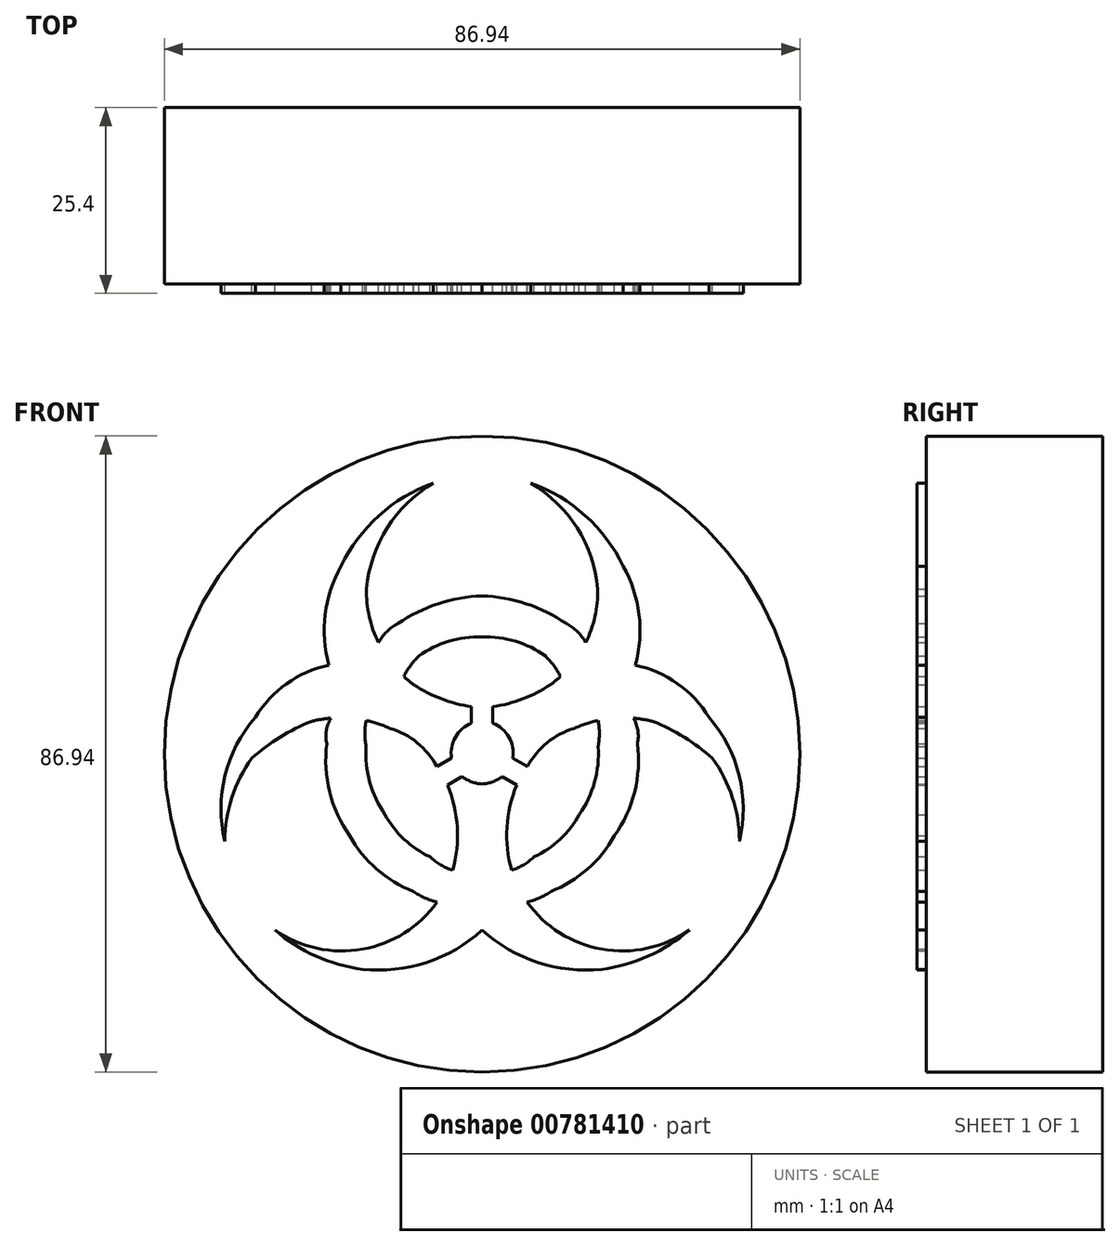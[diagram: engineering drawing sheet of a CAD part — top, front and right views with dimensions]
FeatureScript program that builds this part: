
annotation { "Feature Type Name" : "Feature", "Feature Type Description" : "" }
export const myFeature = defineFeature(function(context is Context, id is Id, definition is map)
    precondition{}
    {
        {
            var Q0;
            Q0=qCreatedBy(makeId("Front.planeOp"),FACE);
            var sketch = newSketch(context, id + "F0", { "sketchPlane" : qUnion([Q0])});
            skArc(sketch, "E0", {"start": v(-6.67, 37.02) * mm, "mid": v(-14.1, 32.6) * mm, "end": v(-19.3, 25.67) * mm});
            skArc(sketch, "E1", {"start": v(-19.3, 25.67) * mm, "mid": v(-21.46, 19.06) * mm, "end": v(-20.95, 12.14) * mm});
            skArc(sketch, "E2", {"start": v(-20.95, 12.14) * mm, "mid": v(-26.73, 9.61) * mm, "end": v(-31.03, 5) * mm});
            skArc(sketch, "E3", {"start": v(-31.03, 5) * mm, "mid": v(-35.17, -2.96) * mm, "end": v(-35.2, -11.93) * mm});
            skArc(sketch, "E4", {"start": v(-6.67, 37.02) * mm, "mid": v(-13, 30.9) * mm, "end": v(-15.81, 22.57) * mm});
            skArc(sketch, "E5", {"start": v(-15.81, 22.57) * mm, "mid": v(-14.17, 15.23) * mm, "end": v(-9.34, 9.47) * mm});
            skArc(sketch, "E6", {"start": v(-9.34, 9.47) * mm, "mid": v(-5.56, 7.53) * mm, "end": v(-1.45, 6.47) * mm});
            skLineSegment(sketch, "E7", {"start": v(-1.45, 6.47) * mm, "end": v(-1.45, 4.21) * mm});
            skArc(sketch, "E8", {"start": v(-1.45, 4.21) * mm, "mid": v(-3.66, 2.3) * mm, "end": v(-4.2, -0.59) * mm});
            skLineSegment(sketch, "E9", {"start": v(-4.2, -0.59) * mm, "end": v(-6.2, -1.7) * mm});
            skArc(sketch, "E10", {"start": v(-6.2, -1.7) * mm, "mid": v(-8.9, 1.55) * mm, "end": v(-12.64, 3.52) * mm});
            skArc(sketch, "E11", {"start": v(-12.64, 3.52) * mm, "mid": v(-17.9, 4.89) * mm, "end": v(-23.34, 4.46) * mm});
            skArc(sketch, "E12", {"start": v(-23.34, 4.46) * mm, "mid": v(-27.64, 2.3) * mm, "end": v(-31.5, -0.59) * mm});
            skArc(sketch, "E13", {"start": v(-31.5, -0.59) * mm, "mid": v(-34.24, -5.97) * mm, "end": v(-35.2, -11.93) * mm});
            skArc(sketch, "E14.MirrorCS", {"start": v(6.67, 37.02) * mm, "mid": v(14.1, 32.6) * mm, "end": v(19.3, 25.67) * mm});
            skArc(sketch, "E15.MirrorCS", {"start": v(6.67, 37.02) * mm, "mid": v(13, 30.9) * mm, "end": v(15.81, 22.57) * mm});
            skArc(sketch, "E16.MirrorCS", {"start": v(15.81, 22.57) * mm, "mid": v(14.17, 15.23) * mm, "end": v(9.34, 9.47) * mm});
            skArc(sketch, "E17.MirrorCS", {"start": v(19.3, 25.67) * mm, "mid": v(21.46, 19.06) * mm, "end": v(20.95, 12.14) * mm});
            skArc(sketch, "E18.MirrorCS", {"start": v(9.34, 9.47) * mm, "mid": v(5.56, 7.53) * mm, "end": v(1.45, 6.47) * mm});
            skArc(sketch, "E19.MirrorCS", {"start": v(6.2, -1.7) * mm, "mid": v(8.9, 1.55) * mm, "end": v(12.64, 3.52) * mm});
            skArc(sketch, "E20.MirrorCS", {"start": v(12.64, 3.52) * mm, "mid": v(17.9, 4.89) * mm, "end": v(23.34, 4.46) * mm});
            skArc(sketch, "E21.MirrorCS", {"start": v(23.34, 4.46) * mm, "mid": v(27.64, 2.3) * mm, "end": v(31.5, -0.59) * mm});
            skArc(sketch, "E22.MirrorCS", {"start": v(20.95, 12.14) * mm, "mid": v(26.73, 9.61) * mm, "end": v(31.03, 5) * mm});
            skArc(sketch, "E23.MirrorCS", {"start": v(31.03, 5) * mm, "mid": v(35.17, -2.96) * mm, "end": v(35.2, -11.93) * mm});
            skArc(sketch, "E24.MirrorCS", {"start": v(31.5, -0.59) * mm, "mid": v(34.24, -5.97) * mm, "end": v(35.2, -11.93) * mm});
            skLineSegment(sketch, "E25.MirrorCS", {"start": v(4.2, -0.59) * mm, "end": v(6.2, -1.7) * mm});
            skArc(sketch, "E26.MirrorCS", {"start": v(1.45, 4.21) * mm, "mid": v(3.66, 2.3) * mm, "end": v(4.2, -0.59) * mm});
            skLineSegment(sketch, "E27.MirrorCS", {"start": v(1.45, 6.47) * mm, "end": v(1.45, 4.21) * mm});
            skArc(sketch, "E28", {"start": v(0, 21.6) * mm, "mid": v(-6.03, 20.54) * mm, "end": v(-11.5, 17.82) * mm});
            skArc(sketch, "E29.MirrorCS", {"start": v(0, 21.6) * mm, "mid": v(6.03, 20.54) * mm, "end": v(11.5, 17.82) * mm});
            skArc(sketch, "E30", {"start": v(-11.5, 17.82) * mm, "mid": v(-13.04, 16.72) * mm, "end": v(-14.17, 15.23) * mm});
            skArc(sketch, "E31", {"start": v(0, 15.99) * mm, "mid": v(-4.55, 15.42) * mm, "end": v(-8.66, 13.38) * mm});
            skArc(sketch, "E32", {"start": v(-8.66, 13.38) * mm, "mid": v(-9.8, 12.08) * mm, "end": v(-10.7, 10.6) * mm});
            skArc(sketch, "E33.MirrorCS", {"start": v(0, 15.99) * mm, "mid": v(4.55, 15.42) * mm, "end": v(8.66, 13.38) * mm});
            skArc(sketch, "E34.MirrorCS", {"start": v(8.66, 13.38) * mm, "mid": v(9.8, 12.08) * mm, "end": v(10.7, 10.6) * mm});
            skArc(sketch, "E35.MirrorCS", {"start": v(11.5, 17.82) * mm, "mid": v(13.04, 16.72) * mm, "end": v(14.17, 15.23) * mm});
            skArc(sketch, "E36", {"start": v(-4.04, -15.94) * mm, "mid": v(-3.4, -10.05) * mm, "end": v(-4.73, -4.28) * mm});
            skArc(sketch, "E37", {"start": v(-16.35, -26.67) * mm, "mid": v(-8.7, -23.03) * mm, "end": v(-4.04, -15.94) * mm});
            skArc(sketch, "E38", {"start": v(-28.34, -24.07) * mm, "mid": v(-22.6, -26.57) * mm, "end": v(-16.35, -26.67) * mm});
            skArc(sketch, "E39", {"start": v(-28.34, -24.07) * mm, "mid": v(-22.75, -27.64) * mm, "end": v(-16.35, -29.43) * mm});
            skArc(sketch, "E40", {"start": v(-16.35, -29.43) * mm, "mid": v(-7.6, -28.5) * mm, "end": v(0, -24.07) * mm});
            skArc(sketch, "E41", {"start": v(-2.78, -3.08) * mm, "mid": v(-1.46, -3.79) * mm, "end": v(0, -4.1) * mm});
            skLineSegment(sketch, "E42", {"start": v(-4.73, -4.28) * mm, "end": v(-2.78, -3.08) * mm});
            skArc(sketch, "E43.MirrorCS", {"start": v(2.78, -3.08) * mm, "mid": v(1.46, -3.79) * mm, "end": v(0, -4.1) * mm});
            skLineSegment(sketch, "E44.MirrorCS", {"start": v(4.73, -4.28) * mm, "end": v(2.78, -3.08) * mm});
            skArc(sketch, "E45.MirrorCS", {"start": v(4.04, -15.94) * mm, "mid": v(3.4, -10.05) * mm, "end": v(4.73, -4.28) * mm});
            skArc(sketch, "E46.MirrorCS", {"start": v(16.35, -26.67) * mm, "mid": v(8.7, -23.03) * mm, "end": v(4.04, -15.94) * mm});
            skArc(sketch, "E47.MirrorCS", {"start": v(28.34, -24.07) * mm, "mid": v(22.6, -26.57) * mm, "end": v(16.35, -26.67) * mm});
            skArc(sketch, "E48.MirrorCS", {"start": v(28.34, -24.07) * mm, "mid": v(22.75, -27.64) * mm, "end": v(16.35, -29.43) * mm});
            skArc(sketch, "E49.MirrorCS", {"start": v(16.35, -29.43) * mm, "mid": v(7.6, -28.5) * mm, "end": v(0, -24.07) * mm});
            skArc(sketch, "E50", {"start": v(-15.88, 1.03) * mm, "mid": v(-15.37, -3.85) * mm, "end": v(-13.27, -8.29) * mm});
            skArc(sketch, "E51", {"start": v(-13.27, -8.29) * mm, "mid": v(-10.66, -11.67) * mm, "end": v(-7.12, -14.05) * mm});
            skArc(sketch, "E52", {"start": v(-7.12, -14.05) * mm, "mid": v(-5.68, -15.15) * mm, "end": v(-4.03, -15.9) * mm});
            skArc(sketch, "E53", {"start": v(-21.24, 1.42) * mm, "mid": v(-20.85, -5.18) * mm, "end": v(-18.1, -11.2) * mm});
            skArc(sketch, "E54", {"start": v(-18.1, -11.2) * mm, "mid": v(-14.42, -15.75) * mm, "end": v(-9.42, -18.79) * mm});
            skArc(sketch, "E55", {"start": v(-9.42, -18.79) * mm, "mid": v(-7.86, -19.67) * mm, "end": v(-6.17, -20.24) * mm});
            skArc(sketch, "E56", {"start": v(-20.7, 4.9) * mm, "mid": v(-21.3, 3.2) * mm, "end": v(-21.24, 1.42) * mm});
            skArc(sketch, "E57", {"start": v(-15.88, 4.58) * mm, "mid": v(-16.04, 2.8) * mm, "end": v(-15.88, 1.03) * mm});
            skArc(sketch, "E58.MirrorCS", {"start": v(7.12, -14.05) * mm, "mid": v(5.68, -15.15) * mm, "end": v(4.03, -15.9) * mm});
            skArc(sketch, "E59.MirrorCS", {"start": v(9.42, -18.79) * mm, "mid": v(7.86, -19.67) * mm, "end": v(6.17, -20.24) * mm});
            skArc(sketch, "E60.MirrorCS", {"start": v(18.1, -11.2) * mm, "mid": v(14.42, -15.75) * mm, "end": v(9.42, -18.79) * mm});
            skArc(sketch, "E61.MirrorCS", {"start": v(13.27, -8.29) * mm, "mid": v(10.66, -11.67) * mm, "end": v(7.12, -14.05) * mm});
            skArc(sketch, "E62.MirrorCS", {"start": v(21.24, 1.42) * mm, "mid": v(20.85, -5.18) * mm, "end": v(18.1, -11.2) * mm});
            skArc(sketch, "E63.MirrorCS", {"start": v(15.88, 1.03) * mm, "mid": v(15.37, -3.85) * mm, "end": v(13.27, -8.29) * mm});
            skArc(sketch, "E64.MirrorCS", {"start": v(15.88, 4.58) * mm, "mid": v(16.04, 2.8) * mm, "end": v(15.88, 1.03) * mm});
            skArc(sketch, "E65.MirrorCS", {"start": v(20.7, 4.9) * mm, "mid": v(21.3, 3.2) * mm, "end": v(21.24, 1.42) * mm});
            skSolve(sketch);
        }
        {
            var Q0;
            Q0 = qSketchRegion(id + "F0", true);
            extrude(context, id + "F1", {"entities" : qUnion([Q0]), "depth" : 25.4 * mm, "offsetDistance" : 25.4 * mm});
        }
        {
            var Q0;
            Q0=qCreatedBy(makeId("Front.planeOp"),FACE);
            var sketch = newSketch(context, id + "F2", { "sketchPlane" : qUnion([Q0])});
            skCircle(sketch, "E66", {"center": v(0, 0) * mm, "radius": 43.47 * mm});
            skSolve(sketch);
        }
        {
            var Q0;
            Q0 = qSketchRegion(id + "F2", true);
            extrude(context, id + "F3", {"entities" : qUnion([Q0]), "operationType" : NewBodyOperationType.ADD, "depth" : 24.13 * mm, "offsetDistance" : 25.4 * mm});
        }
    });
